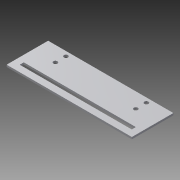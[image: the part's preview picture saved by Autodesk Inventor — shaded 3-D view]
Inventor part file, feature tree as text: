
AUTODESK INVENTOR PART (.ipt)
format: ipt  version: 2015 (Build 190159000, 159)  size: 131,584 bytes
history: native  units: mm
features: sketch x4, extrude x3, other x1, hole x1
ambient origin geometry x8: Origin, YZ Plane, XZ Plane, XY Plane, X Axis, Y Axis, Z Axis, Center Point
bodies: Body1 (feature_tree)
feature tree (9):
  other  "ソリッド1"
  extrude  "押し出し1"  Depth=11.5mm
  extrude  "押し出し2"  Depth=95.0mm
  extrude  "押し出し4"  Depth=1.5mm TaperAngle=0.0deg
  hole  "穴2"  [1 undecoded]
  sketch  "スケッチ1"
  sketch  "スケッチ2"
  sketch  "スケッチ5"
  sketch  "スケッチ6"
note: 1 required parameter value undecoded (feature->parameter linkage not recoverable at this tier; creation-order binding heuristic only, values carry confidence <= 0.55)
